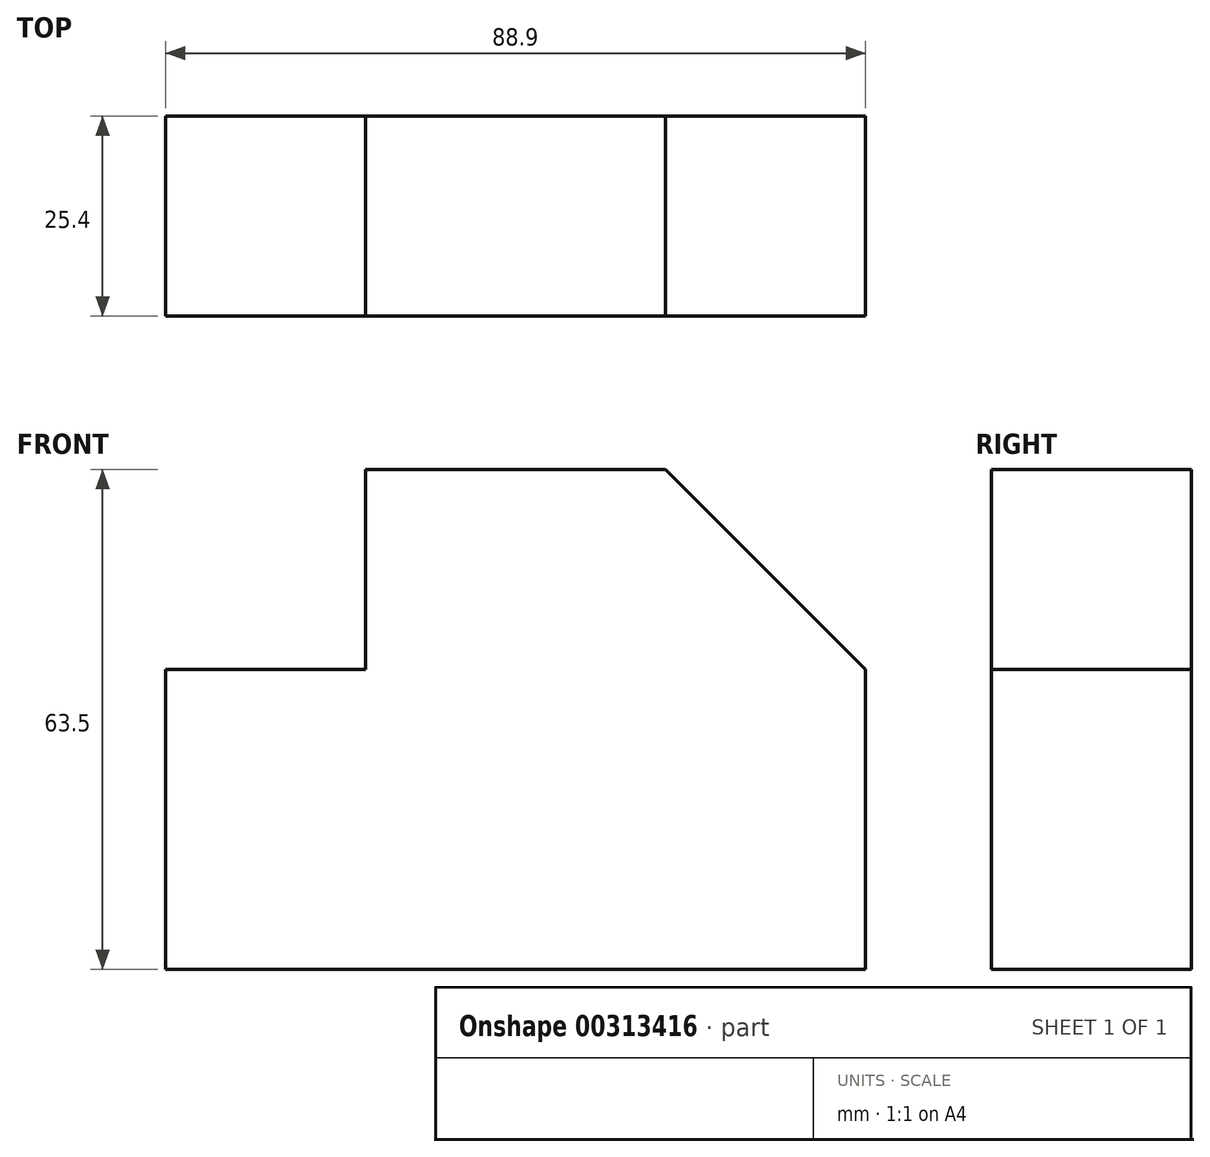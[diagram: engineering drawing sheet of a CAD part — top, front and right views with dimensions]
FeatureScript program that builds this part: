
annotation { "Feature Type Name" : "Feature", "Feature Type Description" : "" }
export const myFeature = defineFeature(function(context is Context, id is Id, definition is map)
    precondition{}
    {
        {
            var Q0;
            Q0=qCreatedBy(makeId("Front.planeOp"),FACE);
            var sketch = newSketch(context, id + "F0", { "sketchPlane" : qUnion([Q0])});
            skLineSegment(sketch, "E0", {"start": v(-34.29, -52.36) * mm, "end": v(54.61, -52.36) * mm});
            skLineSegment(sketch, "E1", {"start": v(54.61, -52.36) * mm, "end": v(54.61, -14.26) * mm});
            skLineSegment(sketch, "E2", {"start": v(-34.29, -52.36) * mm, "end": v(-34.29, -14.26) * mm});
            skLineSegment(sketch, "E3", {"start": v(-34.29, -14.26) * mm, "end": v(-8.89, -14.26) * mm});
            skLineSegment(sketch, "E4", {"start": v(-8.89, -14.26) * mm, "end": v(-8.89, 11.14) * mm});
            skLineSegment(sketch, "E5", {"start": v(-8.89, 11.14) * mm, "end": v(29.21, 11.14) * mm});
            skLineSegment(sketch, "E6", {"start": v(29.21, 11.14) * mm, "end": v(54.61, -14.26) * mm});
            skSolve(sketch);
        }
        {
            var Q0;
            Q0=makeQuery(id+"F0.imprint","IMPRINT",FACE,{"disambiguationData":[TD([[makeQuery(id+"F0.imprint","IMPRINT",EDGE,{"derivedFrom":sQuery(id+"F0.wireOp",EDGE,"E0")}),1.0]])]});
            extrude(context, id + "F1", {"entities" : qUnion([Q0]), "depth" : 25.4 * mm});
        }
    });
